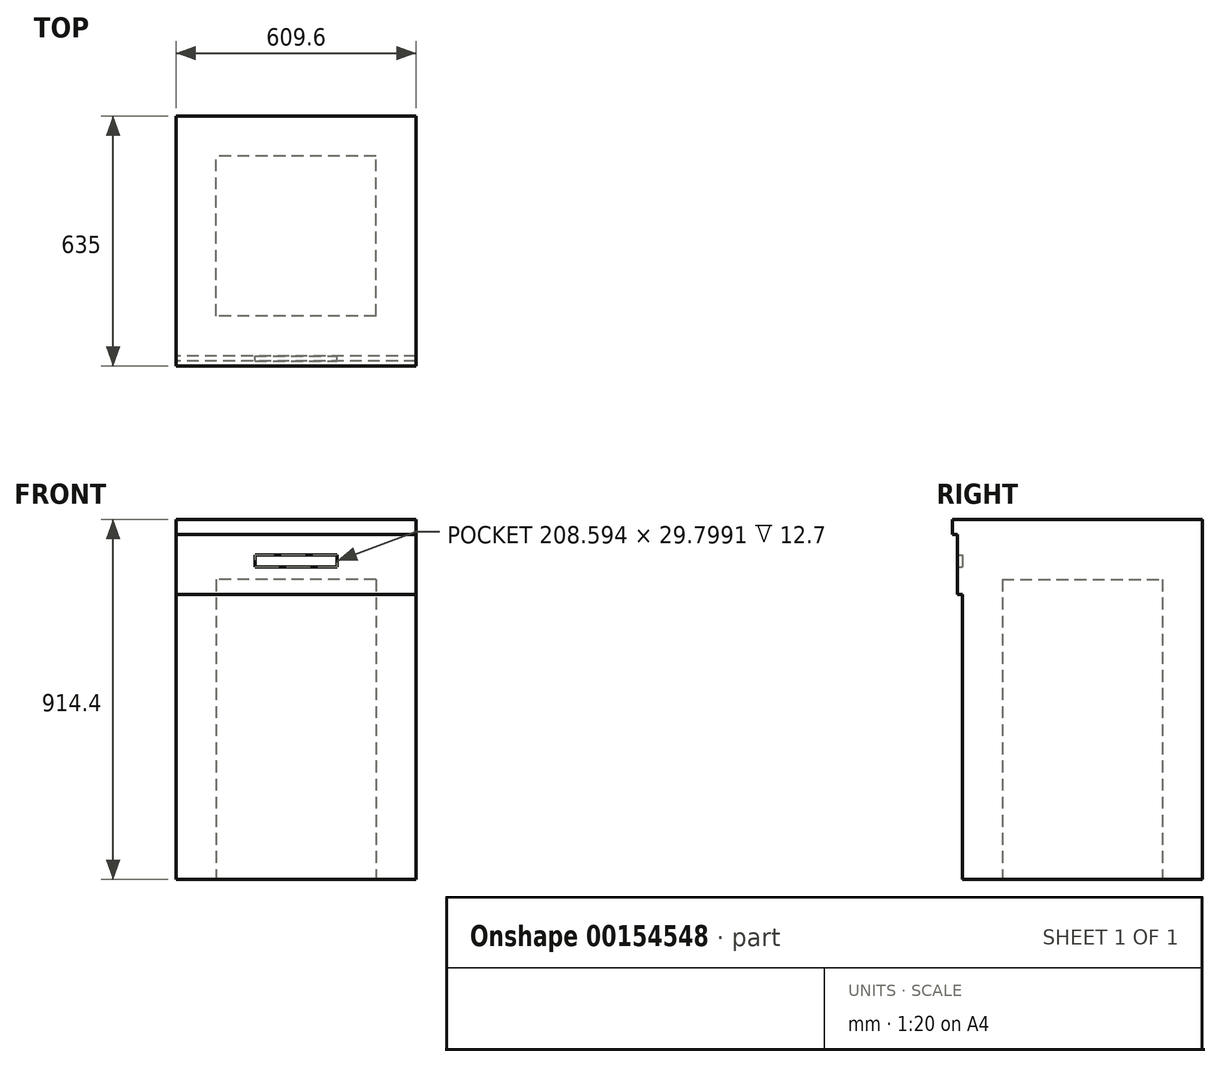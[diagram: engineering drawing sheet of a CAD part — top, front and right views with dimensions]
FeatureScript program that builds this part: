
annotation { "Feature Type Name" : "Feature", "Feature Type Description" : "" }
export const myFeature = defineFeature(function(context is Context, id is Id, definition is map)
    precondition{}
    {
        {
            var Q0;
            Q0=qCreatedBy(makeId("Top.planeOp"),FACE);
            var sketch = newSketch(context, id + "F0", { "sketchPlane" : qUnion([Q0])});
            skLineSegment(sketch, "E0.bottom", {"start": v(304.8, 304.8) * mm, "end": v(-304.8, 304.8) * mm});
            skLineSegment(sketch, "E0.top", {"start": v(304.8, -304.8) * mm, "end": v(-304.8, -304.8) * mm});
            skLineSegment(sketch, "E0.left", {"start": v(304.8, 304.8) * mm, "end": v(304.8, -304.8) * mm});
            skLineSegment(sketch, "E0.right", {"start": v(-304.8, 304.8) * mm, "end": v(-304.8, -304.8) * mm});
            skPoint(sketch, "E0.middle", {"position": v(0, 0) * mm});
            skSolve(sketch);
        }
        {
            var Q0;
            Q0=makeQuery(id+"F0.imprint","IMPRINT",FACE,{"disambiguationData":[TD([[makeQuery(id+"F0.imprint","IMPRINT",EDGE,{"derivedFrom":sQuery(id+"F0.wireOp",EDGE,"E0.bottom")}),1.0]])]});
            extrude(context, id + "F1", {"entities" : qUnion([Q0]), "depth" : 914.4 * mm});
        }
        {
            var Q0;
            Q0=makeQuery(id+"F1.opExtrude","CAP_FACE",FACE,{"disambiguationData":[OSD([sQuery(id+"F0.wireOp",EDGE,"E0.bottom"),sQuery(id+"F0.wireOp",EDGE,"E0.top"),sQuery(id+"F0.wireOp",EDGE,"E0.left"),sQuery(id+"F0.wireOp",EDGE,"E0.right")])],"isStart":false});
            var sketch = newSketch(context, id + "F2", { "sketchPlane" : qUnion([Q0])});
            skLineSegment(sketch, "E1.bottom", {"start": v(-304.8, 304.8) * mm, "end": v(304.8, 304.8) * mm});
            skLineSegment(sketch, "E1.top", {"start": v(-304.8, -330.2) * mm, "end": v(304.8, -330.2) * mm});
            skLineSegment(sketch, "E1.left", {"start": v(-304.8, 304.8) * mm, "end": v(-304.8, -330.2) * mm});
            skLineSegment(sketch, "E1.right", {"start": v(304.8, 304.8) * mm, "end": v(304.8, -330.2) * mm});
            skSolve(sketch);
        }
        {
            var Q0;
            {var subQ0=sQuery(id+"F2.wireOp",EDGE,"E1.bottom");Q0=makeQuery(id+"F2.imprint","IMPRINT",FACE,{"disambiguationData":[TD([[makeQuery(id+"F2.imprint","IMPRINT",EDGE,{"derivedFrom":subQ0}),1.0]])]});}
            var Q1;
            {var subQ0=sQuery(id+"F2.wireOp",EDGE,"E1.top");Q1=makeQuery(id+"F2.imprint","IMPRINT",FACE,{"disambiguationData":[TD([[makeQuery(id+"F2.imprint","IMPRINT",EDGE,{"derivedFrom":subQ0}),1.0]])]});}
            extrude(context, id + "F3", {"entities" : qUnion([Q0, Q1]), "operationType" : NewBodyOperationType.ADD, "oppositeDirection" : true, "depth" : 38.1 * mm});
        }
        {
            var Q0;
            Q0=makeQuery(id+"F1.opExtrude","SWEPT_FACE",FACE,{"disambiguationData":[OSD([sQuery(id+"F0.wireOp",EDGE,"E0.top")])]});
            var sketch = newSketch(context, id + "F4", { "sketchPlane" : qUnion([Q0])});
            skLineSegment(sketch, "E2.bottom", {"start": v(-304.8, 876.3) * mm, "end": v(304.8, 876.3) * mm});
            skLineSegment(sketch, "E2.top", {"start": v(-304.8, 723.9) * mm, "end": v(304.8, 723.9) * mm});
            skLineSegment(sketch, "E2.left", {"start": v(-304.8, 876.3) * mm, "end": v(-304.8, 723.9) * mm});
            skLineSegment(sketch, "E2.right", {"start": v(304.8, 876.3) * mm, "end": v(304.8, 723.9) * mm});
            skLineSegment(sketch, "E3.bottom", {"start": v(-104.3, 823.93) * mm, "end": v(104.3, 823.93) * mm});
            skLineSegment(sketch, "E3.top", {"start": v(-104.3, 794.13) * mm, "end": v(104.3, 794.13) * mm});
            skLineSegment(sketch, "E3.left", {"start": v(-104.3, 823.93) * mm, "end": v(-104.3, 794.13) * mm});
            skLineSegment(sketch, "E3.right", {"start": v(104.3, 823.93) * mm, "end": v(104.3, 794.13) * mm});
            skLineSegment(sketch, "E4", {"start": v(0, 794.13) * mm, "end": v(0, 723.9) * mm, "construction": true});
            skSolve(sketch);
        }
        {
            var Q0;
            Q0=makeQuery(id+"F4.imprint","IMPRINT",FACE,{"disambiguationData":[TD([[makeQuery(id+"F4.imprint","IMPRINT",EDGE,{"derivedFrom":sQuery(id+"F4.wireOp",EDGE,"E2.bottom")}),1.0]])]});
            extrude(context, id + "F5", {"entities" : qUnion([Q0]), "operationType" : NewBodyOperationType.ADD, "depth" : 12.7 * mm});
        }
        {
            var Q0;
            Q0=makeQuery(id+"F1.opExtrude","CAP_FACE",FACE,{"disambiguationData":[OSD([sQuery(id+"F0.wireOp",EDGE,"E0.bottom"),sQuery(id+"F0.wireOp",EDGE,"E0.top"),sQuery(id+"F0.wireOp",EDGE,"E0.left"),sQuery(id+"F0.wireOp",EDGE,"E0.right")])],"isStart":true});
            var sketch = newSketch(context, id + "F6", { "sketchPlane" : qUnion([Q0])});
            skLineSegment(sketch, "E5.bottom", {"start": v(203.2, 203.2) * mm, "end": v(-203.2, 203.2) * mm});
            skLineSegment(sketch, "E5.top", {"start": v(203.2, -203.2) * mm, "end": v(-203.2, -203.2) * mm});
            skLineSegment(sketch, "E5.left", {"start": v(203.2, 203.2) * mm, "end": v(203.2, -203.2) * mm});
            skLineSegment(sketch, "E5.right", {"start": v(-203.2, 203.2) * mm, "end": v(-203.2, -203.2) * mm});
            skSolve(sketch);
        }
        {
            var Q0;
            Q0=makeQuery(id+"F6.imprint","IMPRINT",FACE,{"disambiguationData":[TD([[makeQuery(id+"F6.imprint","IMPRINT",EDGE,{"derivedFrom":sQuery(id+"F6.wireOp",EDGE,"E5.bottom")}),1.0]])]});
            extrude(context, id + "F7", {"entities" : qUnion([Q0]), "operationType" : NewBodyOperationType.REMOVE, "oppositeDirection" : true, "depth" : 762 * mm});
        }
    });
